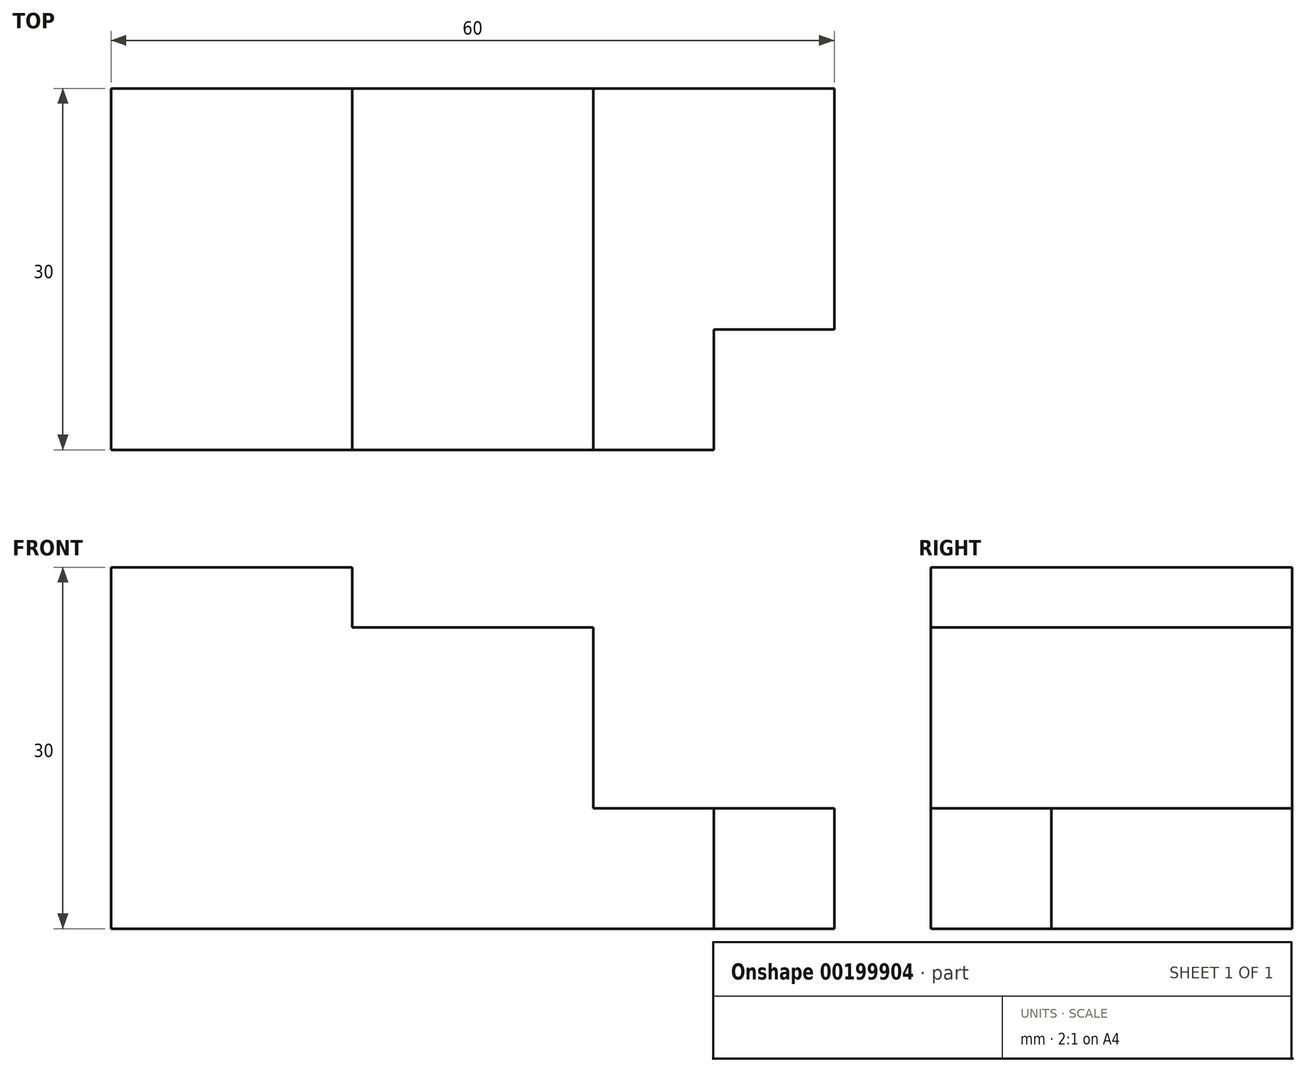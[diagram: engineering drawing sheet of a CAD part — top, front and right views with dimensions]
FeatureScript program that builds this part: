
annotation { "Feature Type Name" : "Feature", "Feature Type Description" : "" }
export const myFeature = defineFeature(function(context is Context, id is Id, definition is map)
    precondition{}
    {
        {
            var Q0;
            Q0=qCreatedBy(makeId("Front.planeOp"),FACE);
            var sketch = newSketch(context, id + "F0", { "sketchPlane" : qUnion([Q0])});
            skLineSegment(sketch, "E0", {"start": v(0, 0) * mm, "end": v(-60, 0) * mm});
            skLineSegment(sketch, "E1", {"start": v(-60, 30) * mm, "end": v(-60, 0) * mm});
            skLineSegment(sketch, "E2", {"start": v(-60, 30) * mm, "end": v(-40, 30) * mm});
            skLineSegment(sketch, "E3", {"start": v(-40, 30) * mm, "end": v(-40, 25) * mm});
            skLineSegment(sketch, "E4", {"start": v(-40, 25) * mm, "end": v(-20, 25) * mm});
            skLineSegment(sketch, "E5", {"start": v(-20, 25) * mm, "end": v(-20, 10) * mm});
            skLineSegment(sketch, "E6", {"start": v(-20, 10) * mm, "end": v(0, 10) * mm});
            skLineSegment(sketch, "E7", {"start": v(0, 10) * mm, "end": v(0, 0) * mm});
            skPoint(sketch, "E8", {"position": v(-10, 10) * mm});
            skLineSegment(sketch, "E9", {"start": v(-10, 10) * mm, "end": v(-10, 0) * mm});
            skSolve(sketch);
        }
        {
            var Q0;
            {var subQ1=sQuery(id+"F0.wireOp",EDGE,"E1");Q0=makeQuery(id+"F0.imprint","IMPRINT",FACE,{"disambiguationData":[TD([[makeQuery(id+"F0.imprint","IMPRINT",EDGE,{"derivedFrom":subQ1}),1.0]])]});}
            extrude(context, id + "F1", {"entities" : qUnion([Q0]), "depth" : 30 * mm});
        }
        {
            var Q0;
            {var subQ0=sQuery(id+"F0.wireOp",EDGE,"E7");Q0=makeQuery(id+"F0.imprint","IMPRINT",FACE,{"disambiguationData":[TD([[makeQuery(id+"F0.imprint","IMPRINT",EDGE,{"derivedFrom":subQ0}),-1.0]])]});}
            extrude(context, id + "F2", {"entities" : qUnion([Q0]), "operationType" : NewBodyOperationType.ADD, "depth" : 20 * mm});
        }
    });
